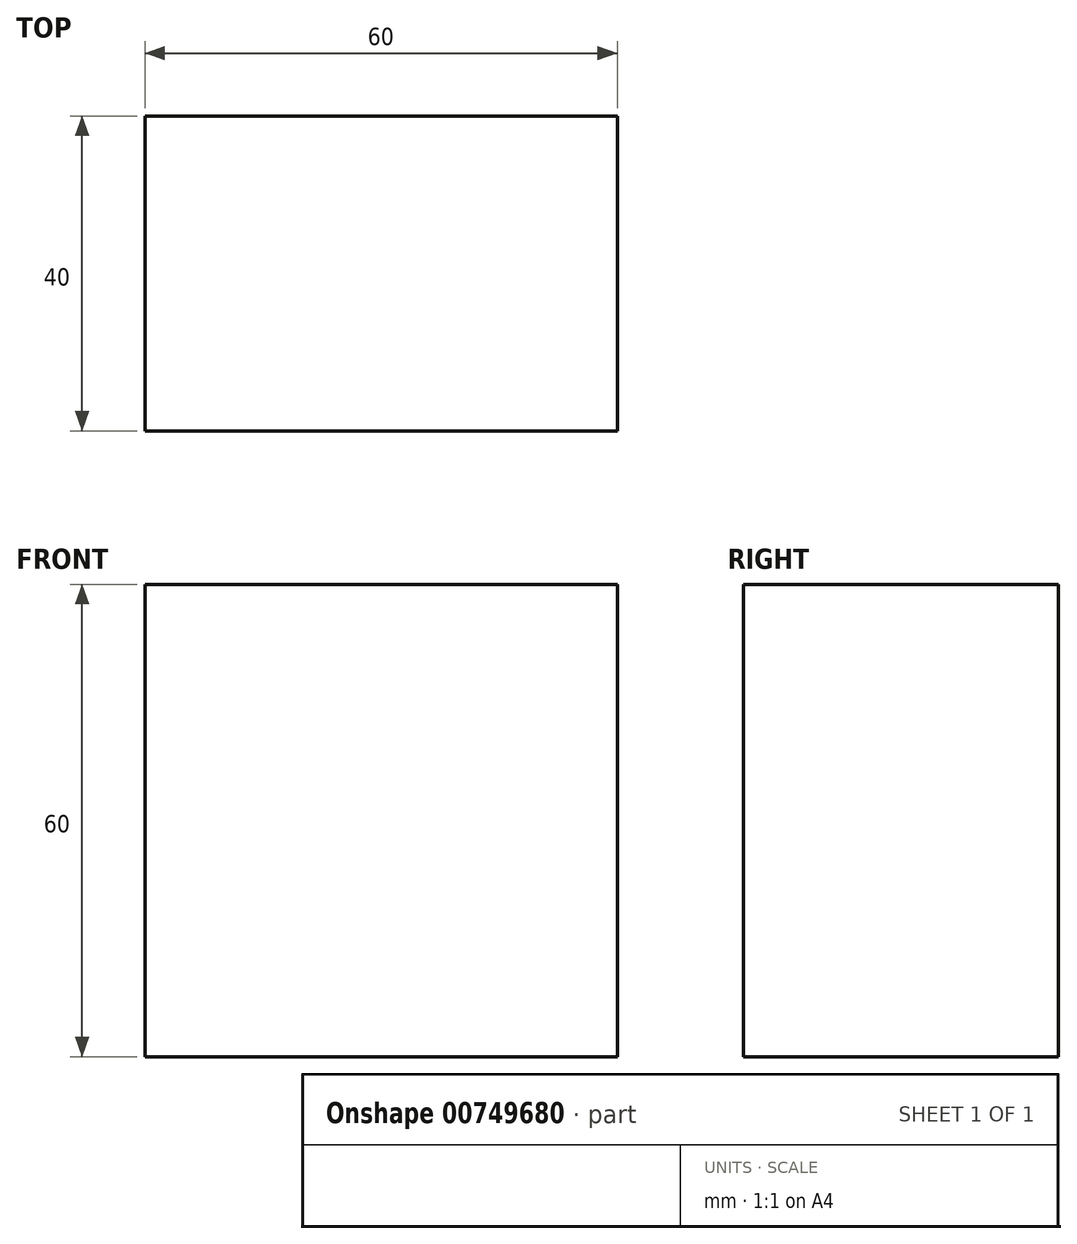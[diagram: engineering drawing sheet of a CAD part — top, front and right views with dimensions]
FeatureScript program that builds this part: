
annotation { "Feature Type Name" : "Feature", "Feature Type Description" : "" }
export const myFeature = defineFeature(function(context is Context, id is Id, definition is map)
    precondition{}
    {
        {
            var Q0;
            Q0=qCreatedBy(makeId("Top.planeOp"),FACE);
            var sketch = newSketch(context, id + "F0", { "sketchPlane" : qUnion([Q0])});
            skLineSegment(sketch, "E0.bottom", {"start": v(0, 0) * mm, "end": v(60, 0) * mm});
            skLineSegment(sketch, "E0.top", {"start": v(0, 40) * mm, "end": v(60, 40) * mm});
            skLineSegment(sketch, "E0.left", {"start": v(0, 0) * mm, "end": v(0, 40) * mm});
            skLineSegment(sketch, "E0.right", {"start": v(60, 0) * mm, "end": v(60, 40) * mm});
            skSolve(sketch);
        }
        {
            var Q0;
            Q0 = qSketchRegion(id + "F0", true);
            extrude(context, id + "F1", {"entities" : qUnion([Q0]), "depth" : 60 * mm, "offsetDistance" : 25 * mm});
        }
    });
